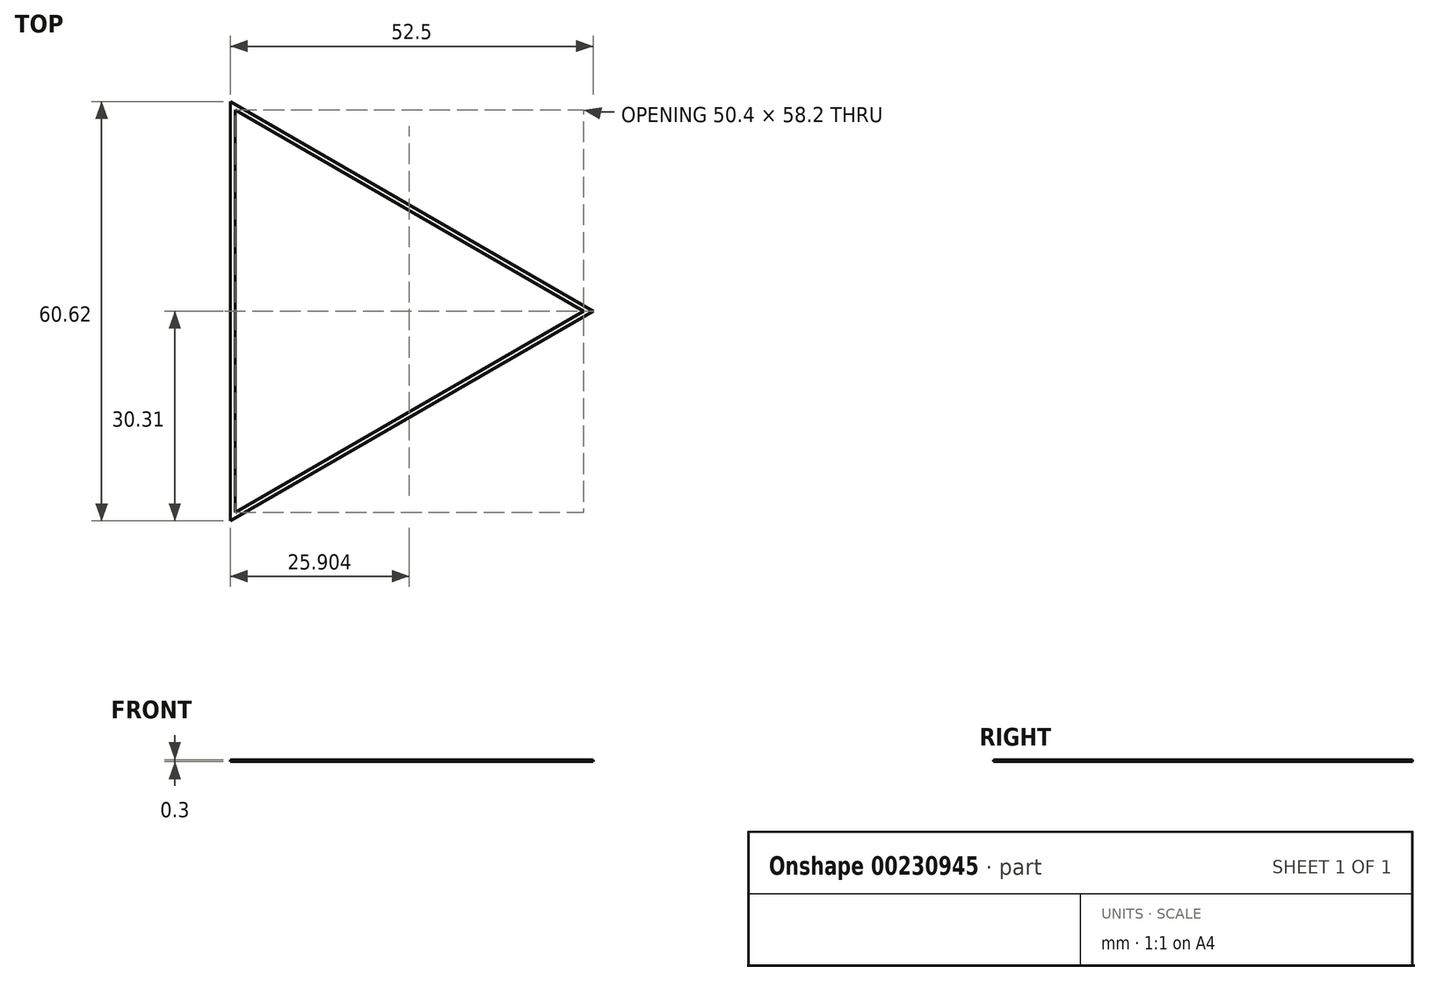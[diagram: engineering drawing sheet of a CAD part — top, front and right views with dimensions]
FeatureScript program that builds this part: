
annotation { "Feature Type Name" : "Feature", "Feature Type Description" : "" }
export const myFeature = defineFeature(function(context is Context, id is Id, definition is map)
    precondition{}
    {
        {
            var Q0;
            Q0=qCreatedBy(makeId("Top.planeOp"),FACE);
            var sketch = newSketch(context, id + "F0", { "sketchPlane" : qUnion([Q0])});
            skCircle(sketch, "E0.cCircle", {"center": v(-45.44, 0) * mm, "radius": 17.5 * mm, "construction": true});
            skLineSegment(sketch, "E0.0", {"start": v(-10.44, 0) * mm, "end": v(-62.94, -30.31) * mm});
            skLineSegment(sketch, "E0.1", {"start": v(-62.94, -30.31) * mm, "end": v(-62.94, 30.31) * mm});
            skLineSegment(sketch, "E0.2", {"start": v(-62.94, 30.31) * mm, "end": v(-10.44, 0) * mm});
            skPoint(sketch, "E0.0.midPoint", {"position": v(-36.69, -15.16) * mm});
            skLineSegment(sketch, "E1.0", {"start": v(-62.24, -29.1) * mm, "end": v(-62.24, 29.1) * mm});
            skLineSegment(sketch, "E1.1", {"start": v(-11.84, 0) * mm, "end": v(-62.24, -29.1) * mm});
            skLineSegment(sketch, "E1.2", {"start": v(-62.24, 29.1) * mm, "end": v(-11.84, 0) * mm});
            skSolve(sketch);
        }
        {
            var Q0;
            Q0=makeQuery(id+"F0.imprint","IMPRINT",FACE,{"disambiguationData":[TD([[makeQuery(id+"F0.imprint","IMPRINT",EDGE,{"derivedFrom":sQuery(id+"F0.wireOp",EDGE,"E0.0")}),-1.0]])]});
            extrude(context, id + "F1", {"entities" : qUnion([Q0]), "depth" : .3 * mm});
        }
    });
